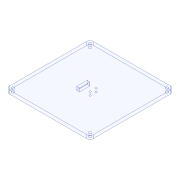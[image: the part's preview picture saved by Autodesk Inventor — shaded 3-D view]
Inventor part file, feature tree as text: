
AUTODESK INVENTOR PART (.ipt)
format: ipt  version: 2020 (Build 240168000, 168)  size: 124,928 bytes
history: native  units: mm
features: extrude x3, sketch x3, fillet x1
ambient origin geometry x8: Origin, YZ Plane, XZ Plane, XY Plane, X Axis, Y Axis, Z Axis, Center Point
bodies: Solid1 (feature_tree)
feature tree (7):
  extrude  "Extrusion1"  Depth=120.0mm
  extrude  "Extrusion2"  Depth=5.0mm
  fillet  "Fillet1"  Radius=110.0mm
  extrude  "Extrusion3"  Depth=4.0mm
  sketch  "Sketch1"  dims[d0=120.0mm d1=120.0mm]
  sketch  "Sketch2"  dims[d2=5.0mm d3=0.0mm d4=110.0mm d5=110.0mm]
  sketch  "Sketch4"  dims[d6=4.0mm d7=4.0mm d8=4.0mm d9=4.0mm d10=5.0mm d11=0.0mm d12=5.0mm d14=4.0mm d15=15.0mm d16=9.5mm d17=14.0mm d18=14.0mm d19=2.5mm d20=2.5mm d21=8.5mm d22=4.25mm d23=10.0mm d24=0.0mm]
